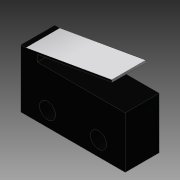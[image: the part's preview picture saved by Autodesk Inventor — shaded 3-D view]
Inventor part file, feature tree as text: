
AUTODESK INVENTOR PART (.ipt)
format: ipt  version: 2015 (Build 190159000, 159)  size: 98,816 bytes
history: native  units: in
note: dims shown in document units (in); Inventor stores cm internally (conversion verified against a paired STEP export)
features: extrude x1, sketch x1
ambient origin geometry x8: Origin, YZ Plane, XZ Plane, XY Plane, X Axis, Y Axis, Z Axis, Center Point
bodies: Solid1 (feature_tree)
feature tree (2):
  extrude  "Extrusion1"  Depth=0.254in
  sketch  "Sketch1"  dims[d2=0.0843in d3=0.1018in d4=0.385in d5=0.5815in d7=0.015in d8=0.0687in d9=0.78in d11=0.435in d12=0.254in d13=0.0in d16=0.12in d17=0.38in d18=0.11in]
